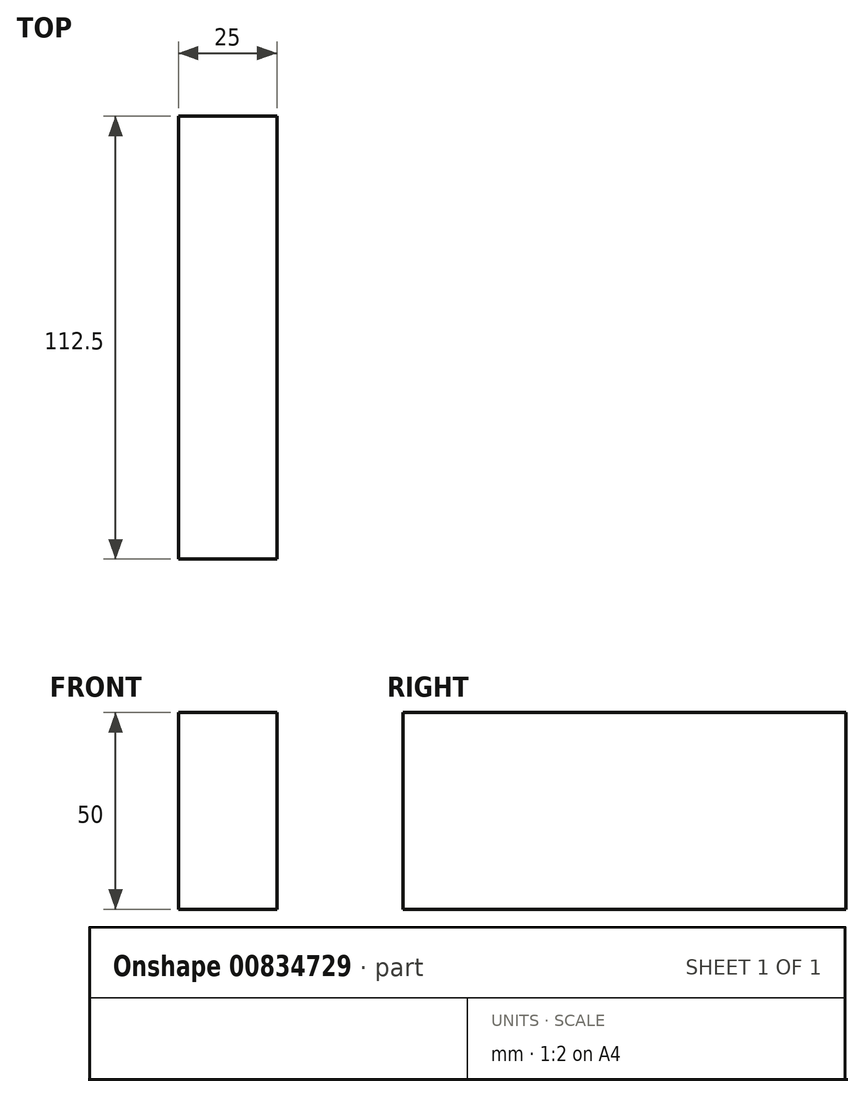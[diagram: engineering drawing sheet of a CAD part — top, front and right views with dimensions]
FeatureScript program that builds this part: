
annotation { "Feature Type Name" : "Feature", "Feature Type Description" : "" }
export const myFeature = defineFeature(function(context is Context, id is Id, definition is map)
    precondition{}
    {
        {
            var Q0;
            Q0=qCreatedBy(makeId("Top.planeOp"),FACE);
            var sketch = newSketch(context, id + "F0", { "sketchPlane" : qUnion([Q0])});
            skLineSegment(sketch, "E0.bottom", {"start": v(-12.5, 56.25) * mm, "end": v(12.5, 56.25) * mm});
            skLineSegment(sketch, "E0.top", {"start": v(-12.5, -56.25) * mm, "end": v(12.5, -56.25) * mm});
            skLineSegment(sketch, "E0.left", {"start": v(-12.5, 56.25) * mm, "end": v(-12.5, -56.25) * mm});
            skLineSegment(sketch, "E0.right", {"start": v(12.5, 56.25) * mm, "end": v(12.5, -56.25) * mm});
            skPoint(sketch, "E0.middle", {"position": v(0, 0) * mm});
            skSolve(sketch);
        }
        {
            var Q0;
            Q0=makeQuery(id+"F0.imprint","IMPRINT",FACE,{"disambiguationData":[TD([[makeQuery(id+"F0.imprint","IMPRINT",EDGE,{"derivedFrom":sQuery(id+"F0.wireOp",EDGE,"E0.bottom")}),-1.0]])]});
            extrude(context, id + "F1", {"entities" : qUnion([Q0]), "depth" : 50 * mm, "offsetDistance" : 25 * mm});
        }
    });
